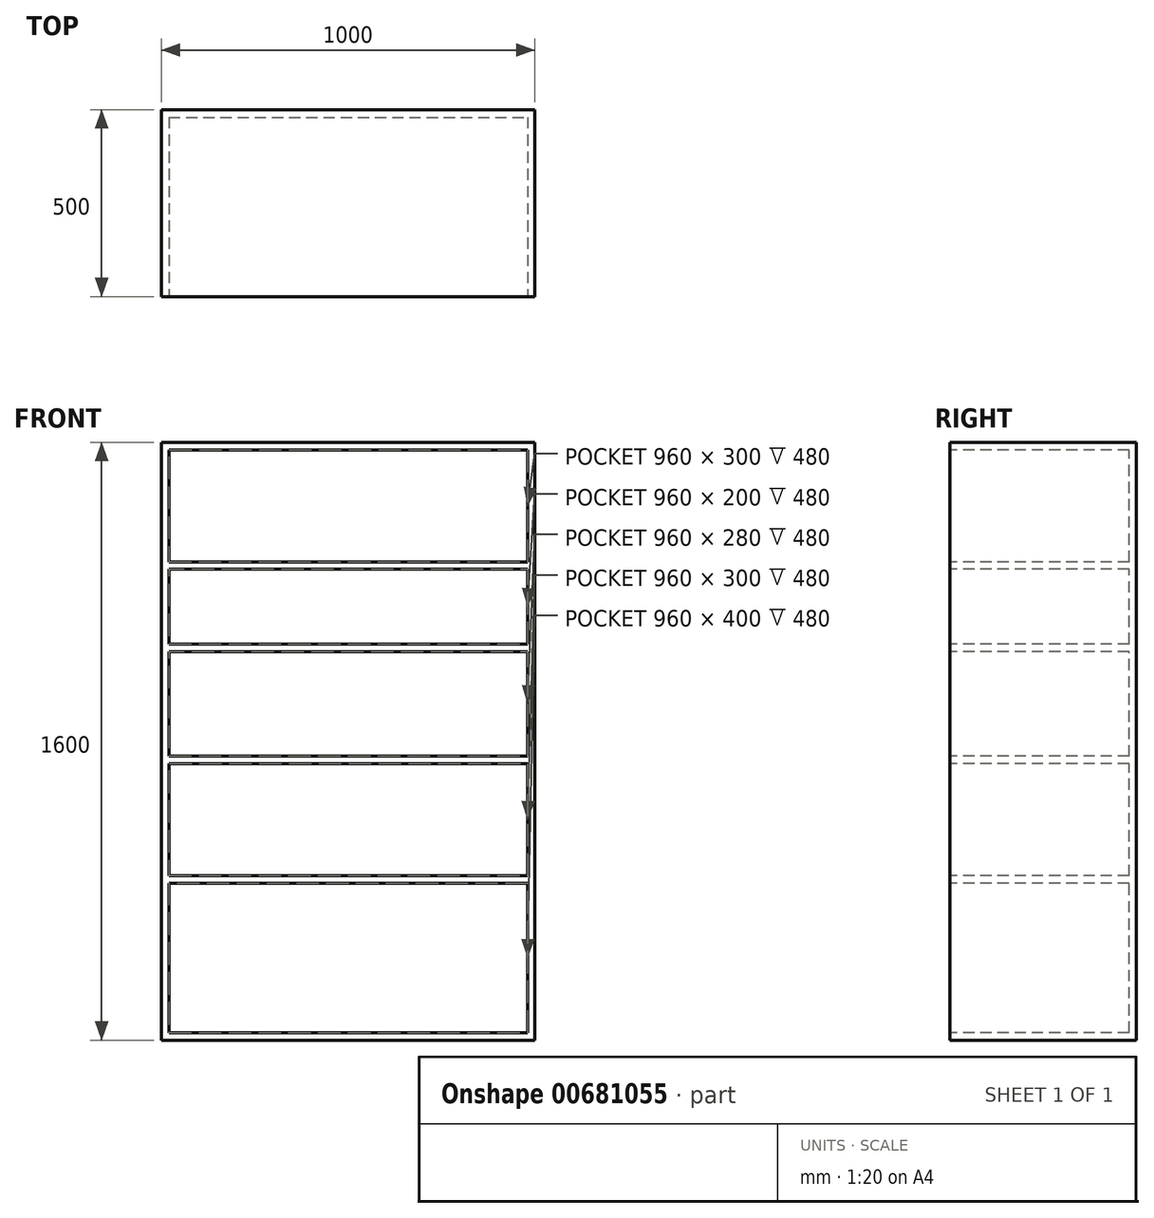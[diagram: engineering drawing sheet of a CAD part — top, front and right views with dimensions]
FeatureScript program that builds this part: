
annotation { "Feature Type Name" : "Feature", "Feature Type Description" : "" }
export const myFeature = defineFeature(function(context is Context, id is Id, definition is map)
    precondition{}
    {
        {
            var Q0;
            Q0=qCreatedBy(makeId("Front.planeOp"),FACE);
            var sketch = newSketch(context, id + "F0", { "sketchPlane" : qUnion([Q0])});
            skLineSegment(sketch, "E0.bottom", {"start": v(0, 0) * mm, "end": v(1000, 0) * mm});
            skLineSegment(sketch, "E0.top", {"start": v(0, 1600) * mm, "end": v(1000, 1600) * mm});
            skLineSegment(sketch, "E0.left", {"start": v(0, 0) * mm, "end": v(0, 1600) * mm});
            skLineSegment(sketch, "E0.right", {"start": v(1000, 0) * mm, "end": v(1000, 1600) * mm});
            skSolve(sketch);
        }
        {
            var Q0;
            Q0 = qSketchRegion(id + "F0", true);
            extrude(context, id + "F1", {"entities" : qUnion([Q0]), "depth" : 500 * mm, "offsetDistance" : 25 * mm});
        }
        {
            var Q0;
            Q0=makeQuery(id+"F1.opExtrude","CAP_FACE",FACE,{"disambiguationData":[OSD([sQuery(id+"F0.wireOp",EDGE,"E0.bottom"),sQuery(id+"F0.wireOp",EDGE,"E0.top"),sQuery(id+"F0.wireOp",EDGE,"E0.left"),sQuery(id+"F0.wireOp",EDGE,"E0.right")])],"isStart":false});
            var sketch = newSketch(context, id + "F2", { "sketchPlane" : qUnion([Q0])});
            skLineSegment(sketch, "E1.bottom", {"start": v(20, 20) * mm, "end": v(980, 20) * mm});
            skLineSegment(sketch, "E1.top", {"start": v(20, 420) * mm, "end": v(980, 420) * mm});
            skLineSegment(sketch, "E1.left", {"start": v(20, 20) * mm, "end": v(20, 420) * mm});
            skLineSegment(sketch, "E1.right", {"start": v(980, 20) * mm, "end": v(980, 420) * mm});
            skLineSegment(sketch, "E2.bottom", {"start": v(20, 440) * mm, "end": v(980, 440) * mm});
            skLineSegment(sketch, "E2.top", {"start": v(20, 740) * mm, "end": v(980, 740) * mm});
            skLineSegment(sketch, "E2.left", {"start": v(20, 440) * mm, "end": v(20, 740) * mm});
            skLineSegment(sketch, "E2.right", {"start": v(980, 440) * mm, "end": v(980, 740) * mm});
            skLineSegment(sketch, "E3.bottom", {"start": v(20, 760) * mm, "end": v(980, 760) * mm});
            skLineSegment(sketch, "E3.top", {"start": v(20, 1040) * mm, "end": v(980, 1040) * mm});
            skLineSegment(sketch, "E3.left", {"start": v(20, 760) * mm, "end": v(20, 1040) * mm});
            skLineSegment(sketch, "E3.right", {"start": v(980, 760) * mm, "end": v(980, 1040) * mm});
            skLineSegment(sketch, "E4.bottom", {"start": v(20, 1060) * mm, "end": v(980, 1060) * mm});
            skLineSegment(sketch, "E4.top", {"start": v(20, 1260) * mm, "end": v(980, 1260) * mm});
            skLineSegment(sketch, "E4.left", {"start": v(20, 1060) * mm, "end": v(20, 1260) * mm});
            skLineSegment(sketch, "E4.right", {"start": v(980, 1060) * mm, "end": v(980, 1260) * mm});
            skLineSegment(sketch, "E5.bottom", {"start": v(20, 1280) * mm, "end": v(980, 1280) * mm});
            skLineSegment(sketch, "E5.top", {"start": v(20, 1580) * mm, "end": v(980, 1580) * mm});
            skLineSegment(sketch, "E5.left", {"start": v(20, 1280) * mm, "end": v(20, 1580) * mm});
            skLineSegment(sketch, "E5.right", {"start": v(980, 1280) * mm, "end": v(980, 1580) * mm});
            skSolve(sketch);
        }
        {
            var Q0;
            Q0 = qSketchRegion(id + "F2", true);
            extrude(context, id + "F3", {"entities" : qUnion([Q0]), "operationType" : NewBodyOperationType.REMOVE, "oppositeDirection" : true, "depth" : 480 * mm, "offsetDistance" : 25 * mm});
        }
    });
